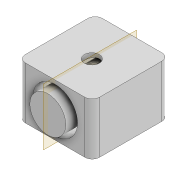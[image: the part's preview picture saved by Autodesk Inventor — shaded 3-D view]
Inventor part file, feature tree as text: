
AUTODESK INVENTOR PART (.ipt)
format: ipt  version: 2022 (Build 260153000, 153)  size: 308,224 bytes
history: native  units: mm
features: extrude x14, sketch x13, projected_geometry x11, chamfer x5, thicken_offset x2, plane x1, fillet x1
ambient origin geometry x8: Origin, YZ Plane, XZ Plane, XY Plane, X Axis, Y Axis, Z Axis, Center Point
bodies: Solid1 (feature_tree)
feature tree (47):
  extrude  "Extrusion1"  Depth=12.2mm
  extrude  "Extrusion2"  Depth=1.0mm
  extrude  "Extrusion3"  Depth=2.0mm TaperAngle=0.0deg
  plane  "Work Plane1"
  extrude  "Extrusion12"  Depth=10.0mm
  fillet  "Fillet5"  Radius=10.0mm
  extrude  "Extrusion14"  Depth=2.0mm
  extrude  "Extrusion15"  Depth=5.0mm TaperAngle=0.0deg
  extrude  "Extrusion16"  Depth=4.1mm
  extrude  "Extrusion17"  Depth=9.0mm
  sketch  "Sketch19"  dims[d79=3.0mm d80=2.0mm]
  extrude  "Extrusion18"  Depth=2.0mm
  extrude  "Extrusion19"  Depth=2.0mm
  thicken_offset  "Thicken1"
  extrude  "Extrusion20"  Depth=3.0mm TaperAngle=0.0deg
  extrude  "Extrusion21"  Depth=1.0mm
  chamfer  "Chamfer1"  Distance=2.0mm
  chamfer  "Chamfer2"  Distance=3.0mm
  chamfer  "Chamfer3"  Distance=2.0mm
  chamfer  "Chamfer4"  Distance=3.0mm
  sketch  "Sketch22"  dims[d86=4.1mm d87=2.0mm d88=3.0mm d89=2.0mm d90=3.0mm d91=2.4mm d92=0.0mm d94=17.0mm d95=2.0mm d96=0.0mm d97=1.5mm d98=2.0mm d99=0.0mm d100=100.0mm d101=0.0mm d102=12.0mm d103=12.0mm d104=3.0mm d105=3.0mm d106=0.0mm d107=3.0mm d108=8.0mm d109=8.0mm d110=3.0mm d111=0.0mm d112=3.0mm d113=5.0mm d114=45.0deg d115=3.0mm d116=5.0mm d117=45.0deg d118=2.0mm d119=3.0mm d120=45.0deg d121=2.0mm d122=3.0mm d123=45.0deg d124=37.0mm d125=19.0mm d126=1.5mm d127=1.5mm d128=30.0mm d130=360.0deg d132=6.0mm d133=0.0mm d134=8.0mm d135=0.0mm d136=2.0mm d137=2.0mm d138=45.0deg d139=2.0mm d140=2.0mm]
  extrude  "Extrusion22"  Depth=2.0mm TaperAngle=0.0deg
  extrude  "Extrusion23"  Depth=2.0mm
  chamfer  "Chamfer5"  Distance=2.0mm
  thicken_offset  "Thicken2"
  sketch  "Sketch1"  dims[d0=9.8mm d1=12.2mm]
  sketch  "Sketch2"  dims[d3=4.0mm d4=1.0mm]
  projected_geometry  "Projected Loop1"
  sketch  "Sketch3"  dims[d5=18.0mm d6=0.0mm d7=2.0mm d8=0.0mm]
  projected_geometry  "Projected Loop2"
  sketch  "Sketch6"  dims[d9=3.0mm d10=0.0mm d49=4.1mm d50=10.0mm]
  projected_geometry  "Projected Loop3"
  projected_geometry  "Projected Loop4"
  sketch  "Sketch14"  dims[d63=100.0mm d64=0.0mm d65=2.0mm]
  sketch  "Sketch15"  dims[d69=7.0mm d71=5.0mm d72=0.0mm]
  projected_geometry  "Projected Loop10"
  projected_geometry  "Projected Loop11"
  sketch  "Sketch16"  dims[d73=16.0mm d74=4.1mm]
  projected_geometry  "Projected Loop12"
  sketch  "Sketch17"  dims[d75=1.4mm d76=9.0mm]
  sketch  "Sketch18"  dims[d77=1.0mm d78=2.0mm]
  projected_geometry  "Projected Loop13"
  projected_geometry  "Projected Loop14"
  projected_geometry  "Projected Loop15"
  sketch  "Sketch20"  dims[d81=4.0mm d82=3.0mm d83=0.0mm]
  sketch  "Sketch21"  dims[d84=1.4mm d85=1.0mm]
  projected_geometry  "Projected Loop16"
